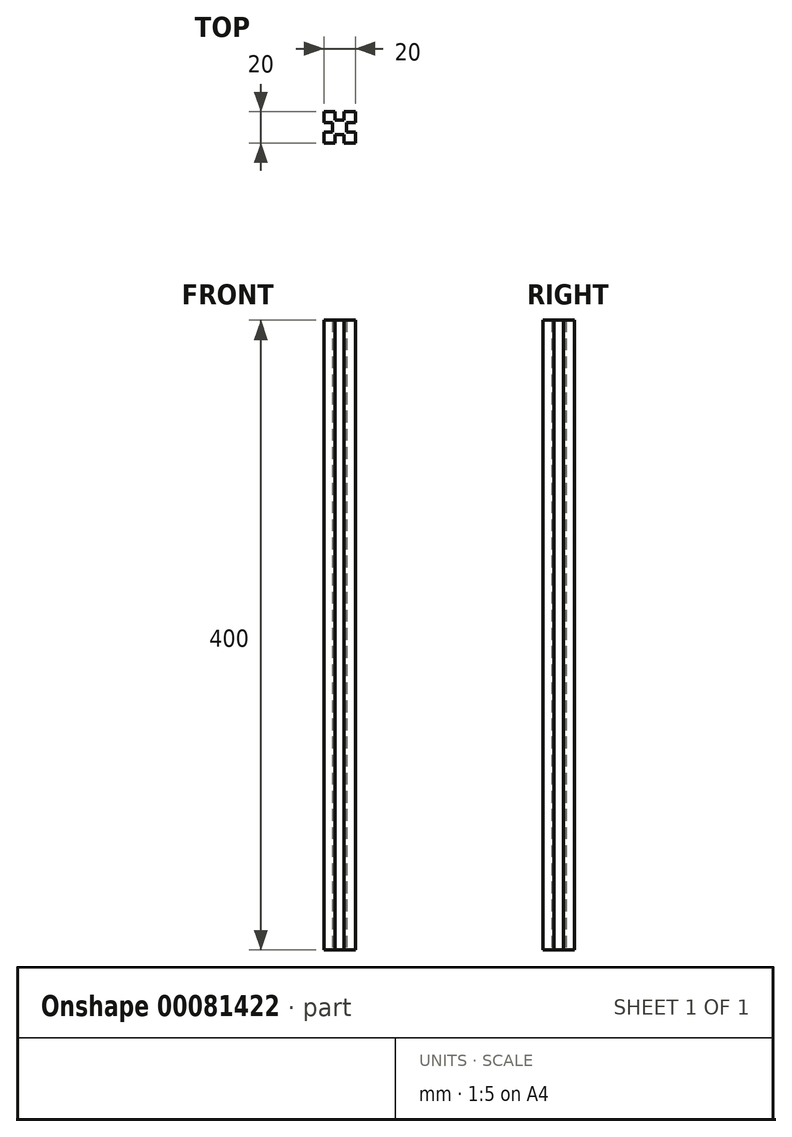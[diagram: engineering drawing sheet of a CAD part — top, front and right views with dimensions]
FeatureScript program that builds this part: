
annotation { "Feature Type Name" : "Feature", "Feature Type Description" : "" }
export const myFeature = defineFeature(function(context is Context, id is Id, definition is map)
    precondition{}
    {
        {
            var Q0;
            Q0=qCreatedBy(makeId("Top.planeOp"),FACE);
            var sketch = newSketch(context, id + "F0", { "sketchPlane" : qUnion([Q0])});
            skLineSegment(sketch, "E0.bottom", {"start": v(-87.17, -55.96) * mm, "end": v(-67.17, -55.96) * mm});
            skLineSegment(sketch, "E0.top", {"start": v(-87.17, -35.96) * mm, "end": v(-67.17, -35.96) * mm});
            skLineSegment(sketch, "E0.left", {"start": v(-87.17, -55.96) * mm, "end": v(-87.17, -35.96) * mm});
            skLineSegment(sketch, "E0.right", {"start": v(-67.17, -55.96) * mm, "end": v(-67.17, -35.96) * mm});
            skLineSegment(sketch, "E1.bottom", {"start": v(-80.17, -35.96) * mm, "end": v(-74.17, -35.96) * mm});
            skLineSegment(sketch, "E1.top", {"start": v(-80.17, -41.46) * mm, "end": v(-74.17, -41.46) * mm});
            skLineSegment(sketch, "E1.left", {"start": v(-80.17, -35.96) * mm, "end": v(-80.17, -41.46) * mm});
            skLineSegment(sketch, "E1.right", {"start": v(-74.17, -35.96) * mm, "end": v(-74.17, -41.46) * mm});
            skLineSegment(sketch, "E2.bottom", {"start": v(-67.17, -42.96) * mm, "end": v(-72.67, -42.96) * mm});
            skLineSegment(sketch, "E2.top", {"start": v(-67.17, -48.96) * mm, "end": v(-72.67, -48.96) * mm});
            skLineSegment(sketch, "E2.left", {"start": v(-67.17, -42.96) * mm, "end": v(-67.17, -48.96) * mm});
            skLineSegment(sketch, "E2.right", {"start": v(-72.67, -42.96) * mm, "end": v(-72.67, -48.96) * mm});
            skLineSegment(sketch, "E3.bottom", {"start": v(-74.17, -55.96) * mm, "end": v(-80.17, -55.96) * mm});
            skLineSegment(sketch, "E3.top", {"start": v(-74.17, -50.46) * mm, "end": v(-80.17, -50.46) * mm});
            skLineSegment(sketch, "E3.left", {"start": v(-74.17, -55.96) * mm, "end": v(-74.17, -50.46) * mm});
            skLineSegment(sketch, "E3.right", {"start": v(-80.17, -55.96) * mm, "end": v(-80.17, -50.46) * mm});
            skLineSegment(sketch, "E4.bottom", {"start": v(-87.17, -48.96) * mm, "end": v(-81.67, -48.96) * mm});
            skLineSegment(sketch, "E4.top", {"start": v(-87.17, -42.96) * mm, "end": v(-81.67, -42.96) * mm});
            skLineSegment(sketch, "E4.left", {"start": v(-87.17, -48.96) * mm, "end": v(-87.17, -42.96) * mm});
            skLineSegment(sketch, "E4.right", {"start": v(-81.67, -48.96) * mm, "end": v(-81.67, -42.96) * mm});
            skSolve(sketch);
        }
        {
            var Q0;
            Q0=makeQuery(id+"F0.imprint","IMPRINT",FACE,{"disambiguationData":[TD([[makeQuery(id+"F0.imprint","IMPRINT",EDGE,{"derivedFrom":sQuery(id+"F0.wireOp",EDGE,"E1.top")}),-1.0]])]});
            extrude(context, id + "F1", {"entities" : qUnion([Q0]), "depth" : 400 * mm});
        }
    });
